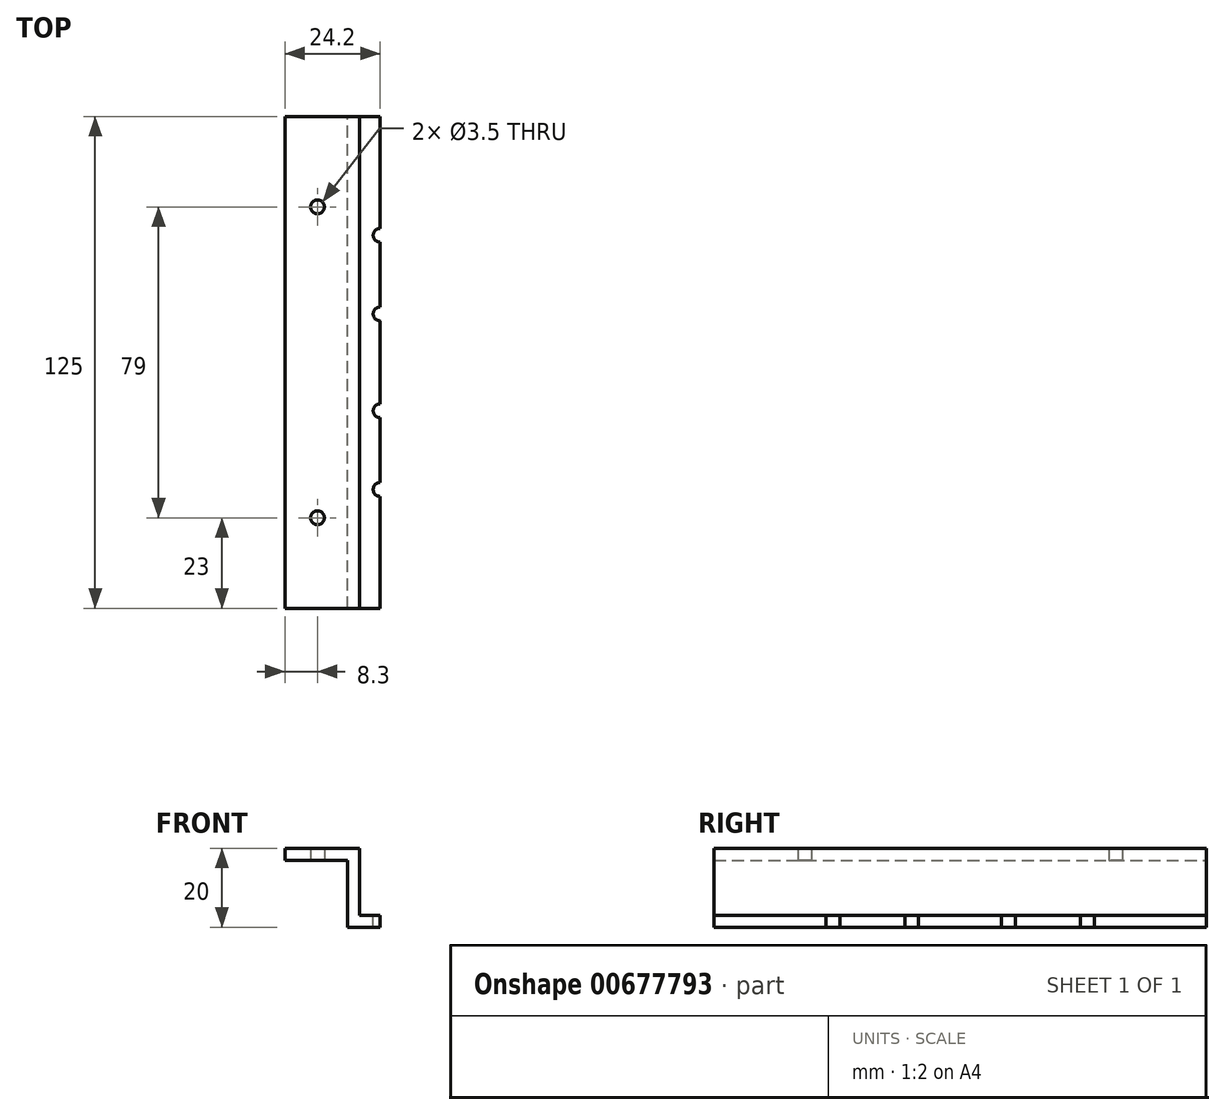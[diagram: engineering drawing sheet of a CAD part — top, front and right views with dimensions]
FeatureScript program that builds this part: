
annotation { "Feature Type Name" : "Feature", "Feature Type Description" : "" }
export const myFeature = defineFeature(function(context is Context, id is Id, definition is map)
    precondition{}
    {
        {
            var Q0;
            Q0=qCreatedBy(makeId("Front.planeOp"),FACE);
            var sketch = newSketch(context, id + "F0", { "sketchPlane" : qUnion([Q0])});
            skLineSegment(sketch, "E0", {"start": v(0, 0) * mm, "end": v(-19, 0) * mm});
            skLineSegment(sketch, "E1", {"start": v(0, 0) * mm, "end": v(0, -17) * mm});
            skLineSegment(sketch, "E2", {"start": v(0, -17) * mm, "end": v(1, -17) * mm});
            skLineSegment(sketch, "E3", {"start": v(1, -17) * mm, "end": v(1, -14) * mm});
            skLineSegment(sketch, "E4", {"start": v(0, -14) * mm, "end": v(1, -14) * mm});
            skLineSegment(sketch, "E5", {"start": v(0, -17) * mm, "end": v(-3, -17) * mm});
            skLineSegment(sketch, "E6", {"start": v(-3, 0) * mm, "end": v(-3, -17) * mm});
            skLineSegment(sketch, "E7", {"start": v(0, 0) * mm, "end": v(0, 3) * mm});
            skLineSegment(sketch, "E8", {"start": v(0, 3) * mm, "end": v(-19, 3) * mm});
            skLineSegment(sketch, "E9", {"start": v(-19, 0) * mm, "end": v(-19, 3) * mm});
            skSolve(sketch);
        }
        {
            var Q0;
            Q0=qCreatedBy(makeId("Top.planeOp"),FACE);
            var sketch = newSketch(context, id + "F1", { "sketchPlane" : qUnion([Q0])});
            skLineSegment(sketch, "E10", {"start": v(0, 0) * mm, "end": v(0, 125) * mm});
            skLineSegment(sketch, "E11", {"start": v(0, 125) * mm, "end": v(-19, 125) * mm});
            skLineSegment(sketch, "E12", {"start": v(-19, 125) * mm, "end": v(-19, 0) * mm});
            skLineSegment(sketch, "E13", {"start": v(-19, 0) * mm, "end": v(-19, 23) * mm});
            skLineSegment(sketch, "E14", {"start": v(-19, 23) * mm, "end": v(-10.7, 23) * mm});
            skCircle(sketch, "E15", {"center": v(-10.7, 23) * mm, "radius": 1.75 * mm});
            skLineSegment(sketch, "E16", {"start": v(-19, 23) * mm, "end": v(-19, 102) * mm});
            skLineSegment(sketch, "E17", {"start": v(-19, 102) * mm, "end": v(-10.7, 102) * mm});
            skCircle(sketch, "E18", {"center": v(-10.7, 102) * mm, "radius": 1.75 * mm});
            skLineSegment(sketch, "E19", {"start": v(0.23, 0) * mm, "end": v(-2.77, 0) * mm});
            skLineSegment(sketch, "E20", {"start": v(-2.77, 0) * mm, "end": v(-2.77, 125) * mm});
            skLineSegment(sketch, "E21", {"start": v(-2.77, 0) * mm, "end": v(-19, 0) * mm});
            skSolve(sketch);
        }
        {
            var Q0;
            Q0=qCreatedBy(makeId("Right.planeOp"),FACE);
            var sketch = newSketch(context, id + "F2", { "sketchPlane" : qUnion([Q0])});
            skLineSegment(sketch, "E22", {"start": v(0, 0) * mm, "end": v(0, -17) * mm});
            skLineSegment(sketch, "E23", {"start": v(0, 0) * mm, "end": v(0, 3) * mm});
            skLineSegment(sketch, "E24", {"start": v(0, 3) * mm, "end": v(125, 3) * mm});
            skLineSegment(sketch, "E25", {"start": v(0, -17) * mm, "end": v(125, -17) * mm});
            skLineSegment(sketch, "E26", {"start": v(125, 3) * mm, "end": v(125, -17) * mm});
            skSolve(sketch);
        }
        {
            var Q0;
            {var subQ0=sQuery(id+"F1.wireOp",EDGE,"E12");Q0=makeQuery(id+"F1.imprint","IMPRINT",FACE,{"disambiguationData":[TD([[makeQuery(id+"F1.imprint","IMPRINT",EDGE,{"derivedFrom":subQ0}),1.0]])]});}
            extrude(context, id + "F3", {"entities" : qUnion([Q0]), "depth" : 3 * mm, "offsetDistance" : 25 * mm});
        }
        {
            var Q0;
            Q0=makeQuery(id+"F2.imprint","IMPRINT",FACE,{"disambiguationData":[TD([[makeQuery(id+"F2.imprint","IMPRINT",EDGE,{"derivedFrom":sQuery(id+"F2.wireOp",EDGE,"E22")}),1.0]])]});
            extrude(context, id + "F4", {"entities" : qUnion([Q0]), "operationType" : NewBodyOperationType.ADD, "depth" : -3 * mm, "offsetDistance" : 25 * mm});
        }
        {
            var Q0;
            {var subQ0=sQuery(id+"F0.wireOp",EDGE,"E2");Q0=makeQuery(id+"F0.imprint","IMPRINT",FACE,{"disambiguationData":[TD([[makeQuery(id+"F0.imprint","IMPRINT",EDGE,{"derivedFrom":subQ0}),1.0]])]});}
            extrude(context, id + "F5", {"entities" : qUnion([Q0]), "operationType" : NewBodyOperationType.ADD, "depth" : -125 * mm, "offsetDistance" : 25 * mm});
        }
        {
            var Q0;
            Q0=makeQuery(id+"F5.opExtrude","SWEPT_FACE",FACE,{"disambiguationData":[OSD([sQuery(id+"F0.wireOp",EDGE,"E4")])]});
            var sketch = newSketch(context, id + "F6", { "sketchPlane" : qUnion([Q0])});
            skLineSegment(sketch, "E27", {"start": v(0, 0) * mm, "end": v(1, 0) * mm});
            skLineSegment(sketch, "E28", {"start": v(0, 0) * mm, "end": v(10, 0) * mm});
            skPoint(sketch, "E28.endSnap0", {"position": v(0.5, 0) * mm});
            skLineSegment(sketch, "E29", {"start": v(1, 125) * mm, "end": v(0, 125) * mm});
            skLineSegment(sketch, "E30", {"start": v(0, 0) * mm, "end": v(0, 125) * mm});
            skLineSegment(sketch, "E31", {"start": v(6.2, 125) * mm, "end": v(1, 125) * mm});
            skLineSegment(sketch, "E32", {"start": v(0, 0) * mm, "end": v(5.2, 0) * mm});
            skLineSegment(sketch, "E33", {"start": v(6.2, 125) * mm, "end": v(5.2, 125) * mm});
            skLineSegment(sketch, "E34", {"start": v(5.2, 0) * mm, "end": v(5.2, 125) * mm});
            skLineSegment(sketch, "E35", {"start": v(5.2, 125) * mm, "end": v(10, 125) * mm});
            skLineSegment(sketch, "E36", {"start": v(10, 125) * mm, "end": v(10, 0) * mm});
            skLineSegment(sketch, "E37", {"start": v(5.2, 0) * mm, "end": v(5.2, 30.2) * mm});
            skLineSegment(sketch, "E38", {"start": v(5.2, 125) * mm, "end": v(5.2, 94.8) * mm});
            skLineSegment(sketch, "E39", {"start": v(5.2, 94.8) * mm, "end": v(5.2, 74.8) * mm});
            skLineSegment(sketch, "E40", {"start": v(5.2, 30.2) * mm, "end": v(5.2, 50.2) * mm});
            skCircle(sketch, "E41", {"center": v(5.2, 30.2) * mm, "radius": 1.75 * mm});
            skCircle(sketch, "E42", {"center": v(5.2, 50.2) * mm, "radius": 1.75 * mm});
            skCircle(sketch, "E43", {"center": v(5.2, 74.8) * mm, "radius": 1.75 * mm});
            skCircle(sketch, "E44", {"center": v(5.2, 94.8) * mm, "radius": 1.75 * mm});
            skLineSegment(sketch, "E45", {"start": v(5.2, 0) * mm, "end": v(1, 0) * mm});
            skLineSegment(sketch, "E46", {"start": v(1, 0) * mm, "end": v(1, 125) * mm});
            skSolve(sketch);
        }
        {
            var Q0;
            {var subQ17=sQuery(id+"F6.wireOp",EDGE,"E31");Q0=makeQuery(id+"F6.imprint","IMPRINT",FACE,{"disambiguationData":[TD([[makeQuery(id+"F6.imprint","IMPRINT",EDGE,{"derivedFrom":subQ17}),1.0]])]});}
            var Q1;
            {var subQ12=sQuery(id+"F6.wireOp",EDGE,"E28");Q1=makeQuery(id+"F6.imprint","IMPRINT",FACE,{"disambiguationData":[TD([[makeQuery(id+"F6.imprint","IMPRINT",EDGE,{"derivedFrom":subQ12}),1.0]])]});}
            extrude(context, id + "F7", {"entities" : qUnion([Q0, Q1]), "operationType" : NewBodyOperationType.ADD, "depth" : -3 * mm, "offsetDistance" : 25 * mm});
        }
    });
